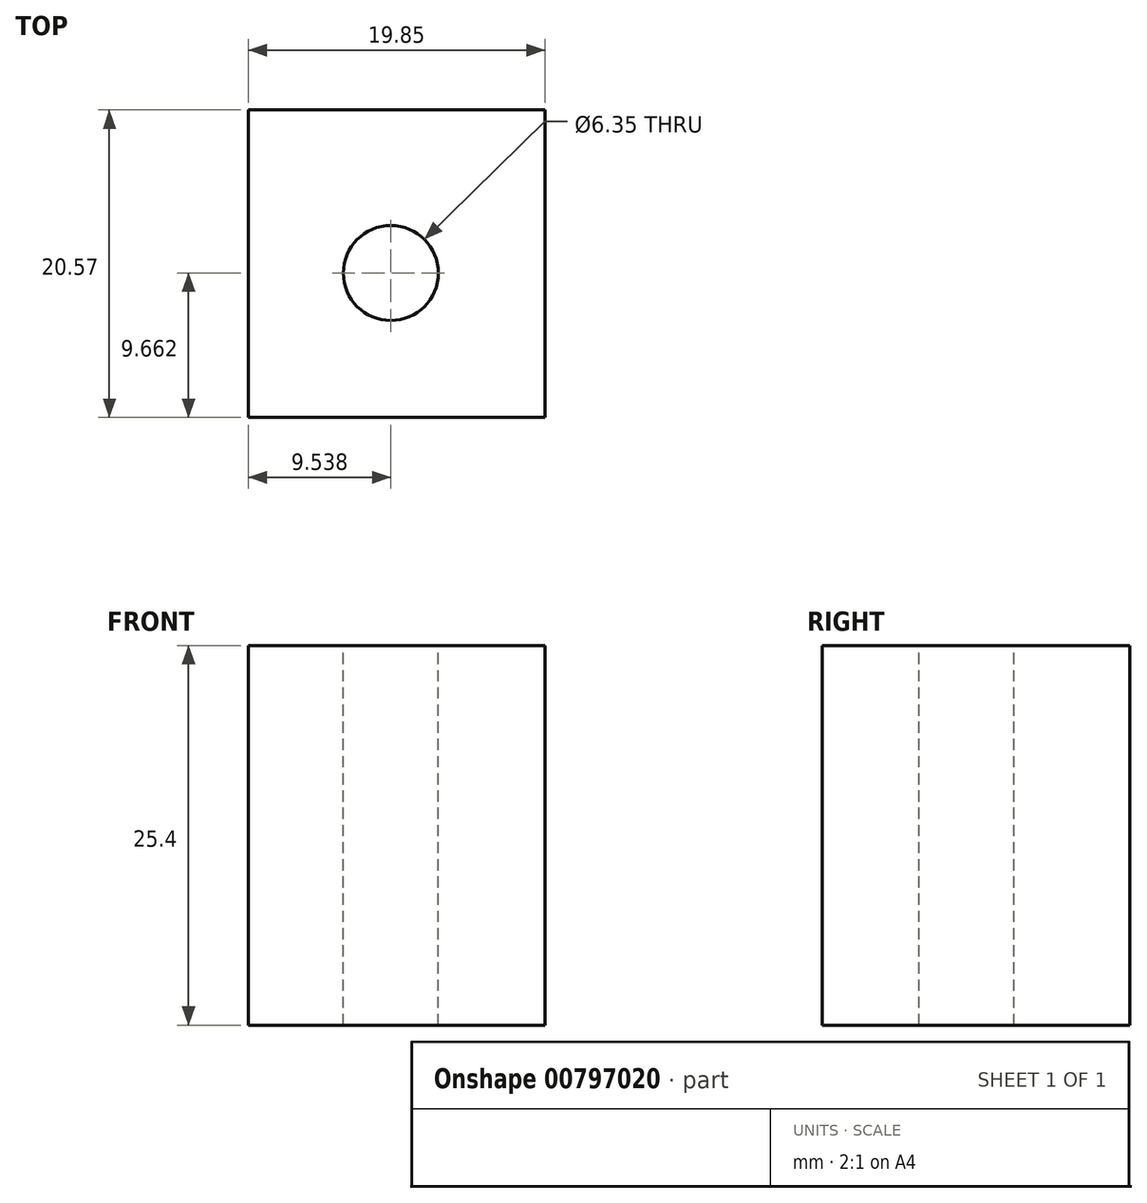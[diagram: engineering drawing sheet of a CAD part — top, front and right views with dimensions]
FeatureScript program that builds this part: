
annotation { "Feature Type Name" : "Feature", "Feature Type Description" : "" }
export const myFeature = defineFeature(function(context is Context, id is Id, definition is map)
    precondition{}
    {
        {
            var Q0;
            Q0=qCreatedBy(makeId("Top.planeOp"),FACE);
            var sketch = newSketch(context, id + "F0", { "sketchPlane" : qUnion([Q0])});
            skLineSegment(sketch, "E0.bottom", {"start": v(0, 0) * mm, "end": v(0, 0) * mm});
            skLineSegment(sketch, "E0.top", {"start": v(0, 15.88) * mm, "end": v(0, 15.88) * mm});
            skLineSegment(sketch, "E0.left", {"start": v(0, 0) * mm, "end": v(0, 15.88) * mm});
            skLineSegment(sketch, "E0.right", {"start": v(0, 0) * mm, "end": v(0, 15.88) * mm});
            skLineSegment(sketch, "E1.bottom", {"start": v(19.85, 7.58) * mm, "end": v(0, 7.58) * mm});
            skLineSegment(sketch, "E1.top", {"start": v(19.85, 28.15) * mm, "end": v(0, 28.15) * mm});
            skLineSegment(sketch, "E1.left", {"start": v(19.85, 7.58) * mm, "end": v(19.85, 28.15) * mm});
            skLineSegment(sketch, "E1.right", {"start": v(0, 7.58) * mm, "end": v(0, 28.15) * mm});
            skSolve(sketch);
        }
        {
            var Q0;
            Q0 = qSketchRegion(id + "F0", true);
            extrude(context, id + "F1", {"entities" : qUnion([Q0]), "depth" : 25.4 * mm, "offsetDistance" : 25.4 * mm});
        }
        {
            var Q0;
            Q0=makeQuery(id+"F1.opExtrude","CAP_FACE",FACE,{"disambiguationData":[OSD([sQuery(id+"F0.wireOp",EDGE,"E1.bottom"),sQuery(id+"F0.wireOp",EDGE,"E1.top"),sQuery(id+"F0.wireOp",EDGE,"E1.left"),sQuery(id+"F0.wireOp",EDGE,"E1.right")])],"isStart":false});
            var sketch = newSketch(context, id + "F2", { "sketchPlane" : qUnion([Q0])});
            skCircle(sketch, "E2", {"center": v(9.54, 17.24) * mm, "radius": 6.42 * mm});
            skSolve(sketch);
        }
        {
            var Q0;
            Q0=sQuery(id+"F2.wireOp",VERTEX,"E2.center");
            var Q1;
            Q1=makeQuery(id+"F1.opExtrude","SWEPT_BODY",BODY,{"disambiguationData":[OSD([sQuery(id+"F0.wireOp",EDGE,"E1.bottom"),sQuery(id+"F0.wireOp",EDGE,"E1.top"),sQuery(id+"F0.wireOp",EDGE,"E1.left"),sQuery(id+"F0.wireOp",EDGE,"E1.right")])]});
            hole(context, id + "F3", {"style" : HoleStyle.SIMPLE, "endStyle" : HoleEndStyle.THROUGH, "holeDiameter" : 6.35 * mm, "majorDiameter" : 6.35 * mm, "isTappedThrough" : true, "tappedDepth" : 12.7 * mm, "tapClearance" : 3, "locations" : qUnion([Q0]), "scope" : qUnion([Q1])});
        }
    });
